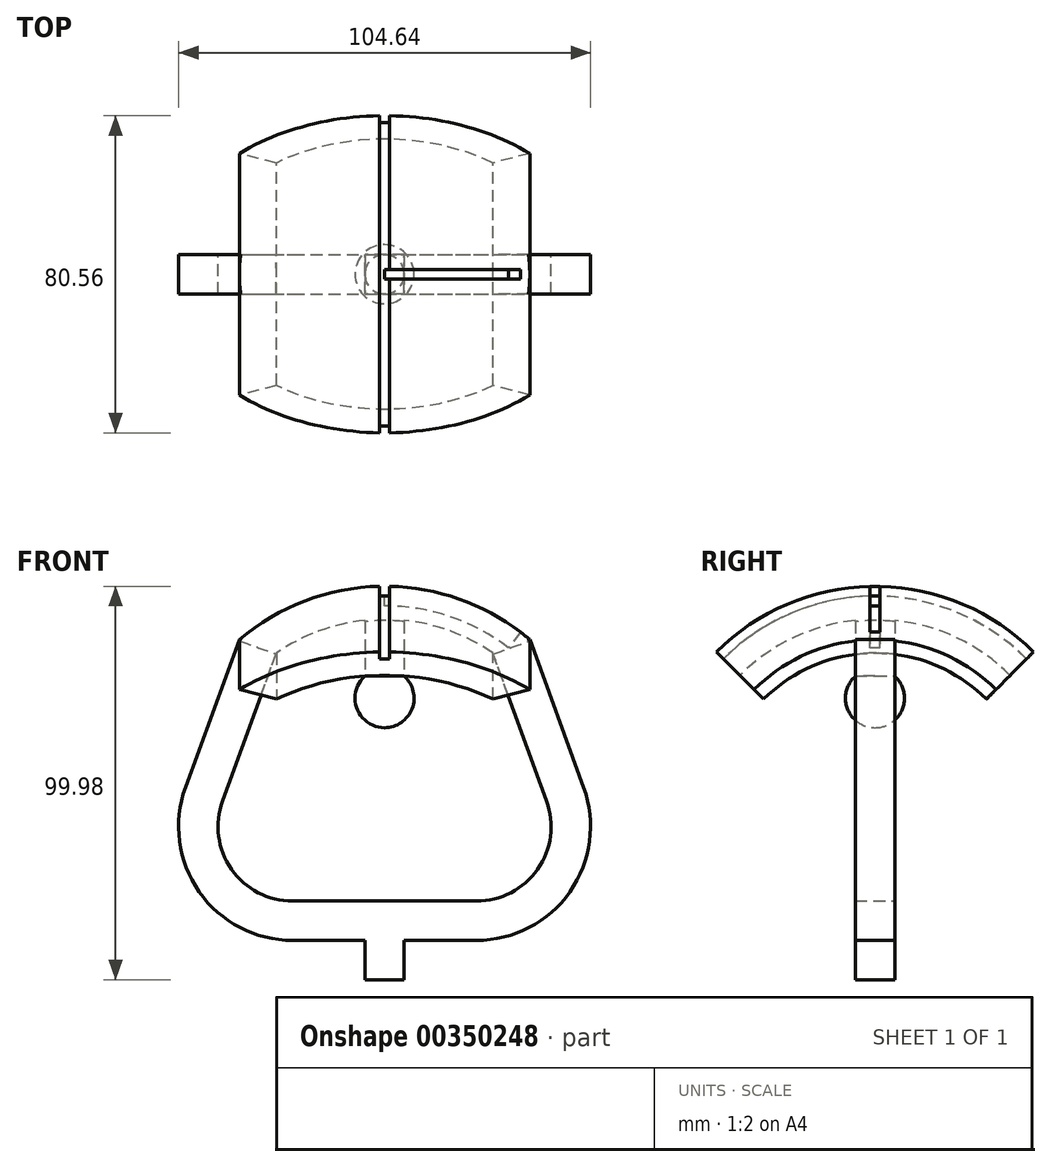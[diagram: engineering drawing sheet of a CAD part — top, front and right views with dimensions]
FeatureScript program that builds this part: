
annotation { "Feature Type Name" : "Feature", "Feature Type Description" : "" }
export const myFeature = defineFeature(function(context is Context, id is Id, definition is map)
    precondition{}
    {
        {
            var Q0;
            Q0=qCreatedBy(makeId("Front.planeOp"),FACE);
            var sketch = newSketch(context, id + "F0", { "sketchPlane" : qUnion([Q0])});
            skLineSegment(sketch, "E0.right", {"start": v(23.38, -33.01) * mm, "end": v(23.38, -23.01) * mm, "construction": true});
            skArc(sketch, "E1", {"start": v(23.38, -23.01) * mm, "mid": v(38.9, -14.93) * mm, "end": v(41.18, 2.41) * mm});
            skArc(sketch, "E2", {"start": v(23.38, -33.01) * mm, "mid": v(47.09, -20.67) * mm, "end": v(50.58, 5.83) * mm});
            skLineSegment(sketch, "E3", {"start": v(38.9, -14.93) * mm, "end": v(47.09, -20.67) * mm, "construction": true});
            skLineSegment(sketch, "E4", {"start": v(41.18, 2.41) * mm, "end": v(50.58, 5.83) * mm, "construction": true});
            skLineSegment(sketch, "E5", {"start": v(41.18, 2.41) * mm, "end": v(27.5, 40) * mm});
            skLineSegment(sketch, "E6", {"start": v(50.58, 5.83) * mm, "end": v(36.9, 43.42) * mm});
            skLineSegment(sketch, "E7", {"start": v(36.9, 43.42) * mm, "end": v(27.5, 40) * mm, "construction": true});
            skLineSegment(sketch, "E8", {"start": v(27.5, 40) * mm, "end": v(-27.5, 40) * mm, "construction": true});
            skLineSegment(sketch, "E9", {"start": v(0, 0) * mm, "end": v(0, 21.04) * mm, "construction": true});
            skLineSegment(sketch, "E10", {"start": v(36.9, 43.42) * mm, "end": v(36.9, 43.42) * mm});
            skArc(sketch, "E11", {"start": v(36.9, 43.42) * mm, "mid": v(0, 56.98) * mm, "end": v(-36.9, 43.42) * mm});
            skArc(sketch, "E12", {"start": v(27.5, 40) * mm, "mid": v(16.77, 45.55) * mm, "end": v(5, 48.28) * mm});
            skLineSegment(sketch, "E13", {"start": v(-36.9, 43.42) * mm, "end": v(-27.5, 40) * mm, "construction": true});
            skLineSegment(sketch, "E14.MirrorCS", {"start": v(-50.58, 5.83) * mm, "end": v(-36.9, 43.42) * mm});
            skLineSegment(sketch, "E15.MirrorCS", {"start": v(-41.18, 2.41) * mm, "end": v(-27.5, 40) * mm});
            skArc(sketch, "E16.MirrorCS", {"start": v(-23.38, -33.01) * mm, "mid": v(-47.09, -20.67) * mm, "end": v(-50.58, 5.83) * mm});
            skArc(sketch, "E17.MirrorCS", {"start": v(-23.38, -23.01) * mm, "mid": v(-38.9, -14.93) * mm, "end": v(-41.18, 2.41) * mm});
            skLineSegment(sketch, "E18", {"start": v(0, 0) * mm, "end": v(38.56, 0) * mm, "construction": true});
            skLineSegment(sketch, "E19", {"start": v(-23.38, -23.01) * mm, "end": v(23.38, -23.01) * mm});
            skLineSegment(sketch, "E20.left", {"start": v(-5, 48.28) * mm, "end": v(-5, 34.13) * mm});
            skLineSegment(sketch, "E20.right", {"start": v(5, 48.54) * mm, "end": v(5, 34.13) * mm});
            skPoint(sketch, "E20.middle", {"position": v(0, 38.28) * mm});
            skLineSegment(sketch, "E21.bottom", {"start": v(5, -33.01) * mm, "end": v(-5, -33.01) * mm, "construction": true});
            skLineSegment(sketch, "E21.top", {"start": v(5, -43.01) * mm, "end": v(-5, -43.01) * mm});
            skLineSegment(sketch, "E21.left", {"start": v(5, -33.01) * mm, "end": v(5, -43.01) * mm});
            skLineSegment(sketch, "E21.right", {"start": v(-5, -33.01) * mm, "end": v(-5, -43.01) * mm});
            skPoint(sketch, "E21.middle", {"position": v(0, -38.01) * mm});
            skLineSegment(sketch, "E22", {"start": v(-23.38, -33.01) * mm, "end": v(-5, -33.01) * mm});
            skLineSegment(sketch, "E23", {"start": v(5, -33.01) * mm, "end": v(23.38, -33.01) * mm});
            skArc(sketch, "E24", {"start": v(-5, 48.28) * mm, "mid": v(-16.77, 45.55) * mm, "end": v(-27.5, 40) * mm});
            skArc(sketch, "E25", {"start": v(5, 48.28) * mm, "mid": v(0, 48.54) * mm, "end": v(-5, 48.28) * mm, "construction": true});
            skArc(sketch, "E26", {"start": v(-5, 34.13) * mm, "mid": v(-7, 25.87) * mm, "end": v(0, 21.04) * mm});
            skArc(sketch, "E27", {"start": v(5, 34.13) * mm, "mid": v(2.68, 35.55) * mm, "end": v(0, 36.04) * mm, "construction": true});
            skLineSegment(sketch, "E28", {"start": v(0, 21.04) * mm, "end": v(0, 36.04) * mm});
            skLineSegment(sketch, "E29", {"start": v(0, 36.04) * mm, "end": v(0, 40) * mm, "construction": true});
            skLineSegment(sketch, "E30", {"start": v(5, 34.13) * mm, "end": v(5, 34.13) * mm});
            skArc(sketch, "E31", {"start": v(0, 21.04) * mm, "mid": v(7, 25.87) * mm, "end": v(5, 34.13) * mm, "construction": true});
            skArc(sketch, "E32", {"start": v(0, 36.04) * mm, "mid": v(-2.68, 35.55) * mm, "end": v(-5, 34.13) * mm, "construction": true});
            skLineSegment(sketch, "E33", {"start": v(-5, 34.13) * mm, "end": v(5, 34.13) * mm});
            skArc(sketch, "E34.0", {"start": v(32.9, 43.42) * mm, "mid": v(0, 54.48) * mm, "end": v(-32.9, 43.42) * mm});
            skLineSegment(sketch, "E35", {"start": v(36.9, 43.42) * mm, "end": v(32.9, 43.42) * mm});
            skLineSegment(sketch, "E36", {"start": v(-32.9, 43.42) * mm, "end": v(-36.9, 43.42) * mm});
            skSolve(sketch);
        }
        {
            var Q0;
            Q0=makeQuery(id+"F0.imprint","IMPRINT",FACE,{"disambiguationData":[TD([[makeQuery(id+"F0.imprint","IMPRINT",EDGE,{"derivedFrom":sQuery(id+"F0.wireOp",EDGE,"E1")}),-1.0]])]});
            extrude(context, id + "F1", {"entities" : qUnion([Q0]), "depth" : 5 * mm, "hasSecondDirection" : true, "secondDirectionOppositeDirection" : true, "secondDirectionDepth" : 5 * mm});
        }
        {
            var Q0;
            Q0=makeQuery(id+"F0.imprint","IMPRINT",FACE,{"disambiguationData":[TD([[makeQuery(id+"F0.imprint","IMPRINT",EDGE,{"derivedFrom":sQuery(id+"F0.wireOp",EDGE,"E26")}),1.0]])]});
            var Q1;
            Q1=sQuery(id+"F0.wireOp",EDGE,"75c9b84a-574a-4500-a7fa-6bebe7ca18a0");
            var Q2;
            Q2=sQuery(id+"F0.wireOp",EDGE,"E9");
            revolve(context, id + "F2", {"operationType" : NewBodyOperationType.ADD, "entities" : qUnion([Q0]), "surfaceEntities" : qUnion([Q1]), "axis" : qUnion([Q2]), "revolveType" : RevolveType.FULL});
        }
        {
            var Q0;
            Q0=qCreatedBy(makeId("Front.planeOp"),FACE);
            var sketch = newSketch(context, id + "F3", { "sketchPlane" : qUnion([Q0])});
            skLineSegment(sketch, "E37.bottom", {"start": v(1.25, 59.48) * mm, "end": v(-1.25, 59.48) * mm});
            skLineSegment(sketch, "E37.top", {"start": v(1.25, 54.48) * mm, "end": v(-1.25, 54.48) * mm});
            skLineSegment(sketch, "E37.left", {"start": v(1.25, 59.48) * mm, "end": v(1.25, 54.48) * mm});
            skLineSegment(sketch, "E37.right", {"start": v(-1.25, 59.48) * mm, "end": v(-1.25, 54.48) * mm});
            skPoint(sketch, "E37.middle", {"position": v(0, 56.98) * mm});
            skArc(sketch, "E38.0", {"start": v(27.5, 40) * mm, "mid": v(16.77, 45.55) * mm, "end": v(5, 48.28) * mm});
            skArc(sketch, "E39.0", {"start": v(-5, 48.28) * mm, "mid": v(-16.77, 45.55) * mm, "end": v(-27.5, 40) * mm});
            skLineSegment(sketch, "E40", {"start": v(36.9, 43.42) * mm, "end": v(27.5, 40) * mm});
            skLineSegment(sketch, "E41", {"start": v(-27.5, 40) * mm, "end": v(-36.9, 43.42) * mm});
            skArc(sketch, "E42", {"start": v(5, 48.28) * mm, "mid": v(0, 48.54) * mm, "end": v(-5, 48.28) * mm});
            skArc(sketch, "E43.0", {"start": v(36.9, 43.42) * mm, "mid": v(0, 56.98) * mm, "end": v(-36.9, 43.42) * mm});
            skSolve(sketch);
        }
        {
            var Q0;
            {var subQ1=sQuery(id+"F3.wireOp",EDGE,"E37.top");Q0=makeQuery(id+"F3.imprint","IMPRINT",FACE,{"disambiguationData":[TD([[makeQuery(id+"F3.imprint","IMPRINT",EDGE,{"derivedFrom":subQ1}),1.0]])]});}
            var Q1;
            Q1=sQuery(id+"F0.wireOp",EDGE,"E18");
            revolve(context, id + "F4", {"operationType" : NewBodyOperationType.ADD, "entities" : qUnion([Q0]), "axis" : qUnion([Q1]), "revolveType" : RevolveType.SYMMETRIC, "angle" : 90 * degree});
        }
        {
            var Q0;
            {var subQ0=sQuery(id+"F3.wireOp",EDGE,"E37.bottom");Q0=makeQuery(id+"F3.imprint","IMPRINT",FACE,{"disambiguationData":[TD([[makeQuery(id+"F3.imprint","IMPRINT",EDGE,{"derivedFrom":subQ0}),1.0]])]});}
            var Q1;
            {var subQ0=sQuery(id+"F3.wireOp",EDGE,"E37.top");Q1=makeQuery(id+"F3.imprint","IMPRINT",FACE,{"disambiguationData":[TD([[makeQuery(id+"F3.imprint","IMPRINT",EDGE,{"derivedFrom":subQ0}),-1.0]])]});}
            var Q2;
            Q2=sQuery(id+"F0.wireOp",EDGE,"E18");
            revolve(context, id + "F5", {"operationType" : NewBodyOperationType.REMOVE, "entities" : qUnion([Q0, Q1]), "axis" : qUnion([Q2]), "revolveType" : RevolveType.SYMMETRIC, "angle" : 90 * degree});
        }
        {
            var Q0;
            Q0=qCreatedBy(makeId("Right.planeOp"),FACE);
            var sketch = newSketch(context, id + "F6", { "sketchPlane" : qUnion([Q0])});
            skPoint(sketch, "E44.0", {"position": v(0, 38.02) * mm});
            skLineSegment(sketch, "E45", {"start": v(0, 0) * mm, "end": v(-39.26, 0) * mm, "construction": true});
            skSolve(sketch);
        }
        {
            var Q0;
            Q0=qCreatedBy(makeId("Front.planeOp"),FACE);
            var sketch = newSketch(context, id + "F7", { "sketchPlane" : qUnion([Q0])});
            skArc(sketch, "E46.0", {"start": v(38.48, 45.35) * mm, "mid": v(0, 59.48) * mm, "end": v(-38.48, 45.35) * mm});
            skArc(sketch, "E47.0", {"start": v(33.63, 39.63) * mm, "mid": v(0, 51.98) * mm, "end": v(-33.63, 39.63) * mm});
            skLineSegment(sketch, "E48", {"start": v(0, 51.98) * mm, "end": v(0, 59.48) * mm});
            skLineSegment(sketch, "E49", {"start": v(36.06, 47.3) * mm, "end": v(31.51, 41.34) * mm});
            skLineSegment(sketch, "E50", {"start": v(38.48, 45.35) * mm, "end": v(33.63, 39.63) * mm, "construction": true});
            skSolve(sketch);
        }
        {
            var Q0;
            Q0 = qSketchRegion(id + "F7", true);
            extrude(context, id + "F8", {"entities" : qUnion([Q0]), "operationType" : NewBodyOperationType.REMOVE, "endBound" : BoundingType.SYMMETRIC, "oppositeDirection" : true, "depth" : 2.5 * mm});
        }
    });
